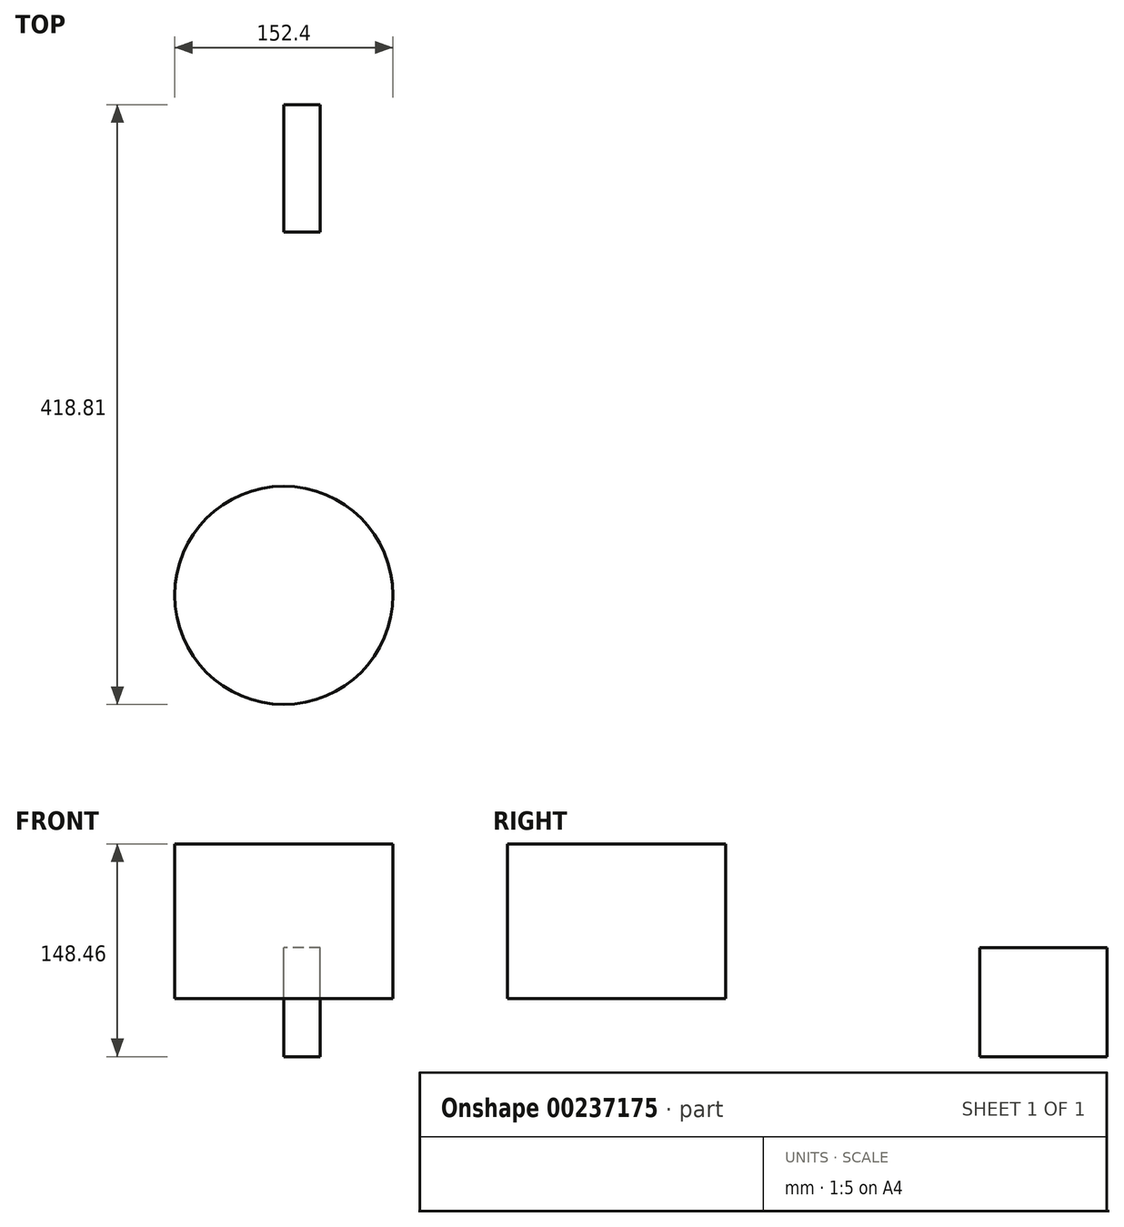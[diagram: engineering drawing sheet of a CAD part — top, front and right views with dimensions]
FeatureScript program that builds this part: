
annotation { "Feature Type Name" : "Feature", "Feature Type Description" : "" }
export const myFeature = defineFeature(function(context is Context, id is Id, definition is map)
    precondition{}
    {
        {
            var Q0;
            Q0=qCreatedBy(makeId("Top.planeOp"),FACE);
            var sketch = newSketch(context, id + "F0", { "sketchPlane" : qUnion([Q0])});
            skCircle(sketch, "E0", {"center": v(0, 0) * mm, "radius": 76.2 * mm});
            skLineSegment(sketch, "E1", {"start": v(0, 0) * mm, "end": v(76.2, 0) * mm});
            skSolve(sketch);
        }
        {
            var Q0;
            Q0 = qSketchRegion(id + "F0", true);
            extrude(context, id + "F1", {"entities" : qUnion([Q0]), "depth" : 107.95 * mm});
        }
        {
            var Q0;
            Q0=qCreatedBy(makeId("Right.planeOp"),FACE);
            var sketch = newSketch(context, id + "F2", { "sketchPlane" : qUnion([Q0])});
            skLineSegment(sketch, "E2.bottom", {"start": v(342.61, -40.51) * mm, "end": v(253.71, -40.51) * mm});
            skLineSegment(sketch, "E2.top", {"start": v(342.61, 35.69) * mm, "end": v(253.71, 35.69) * mm});
            skLineSegment(sketch, "E2.left", {"start": v(342.61, -40.51) * mm, "end": v(342.61, 35.69) * mm});
            skLineSegment(sketch, "E2.right", {"start": v(253.71, -40.51) * mm, "end": v(253.71, 35.69) * mm});
            skSolve(sketch);
        }
        {
            var Q0;
            Q0 = qSketchRegion(id + "F2", true);
            extrude(context, id + "F3", {"entities" : qUnion([Q0]), "depth" : 25.4 * mm});
        }
    });
